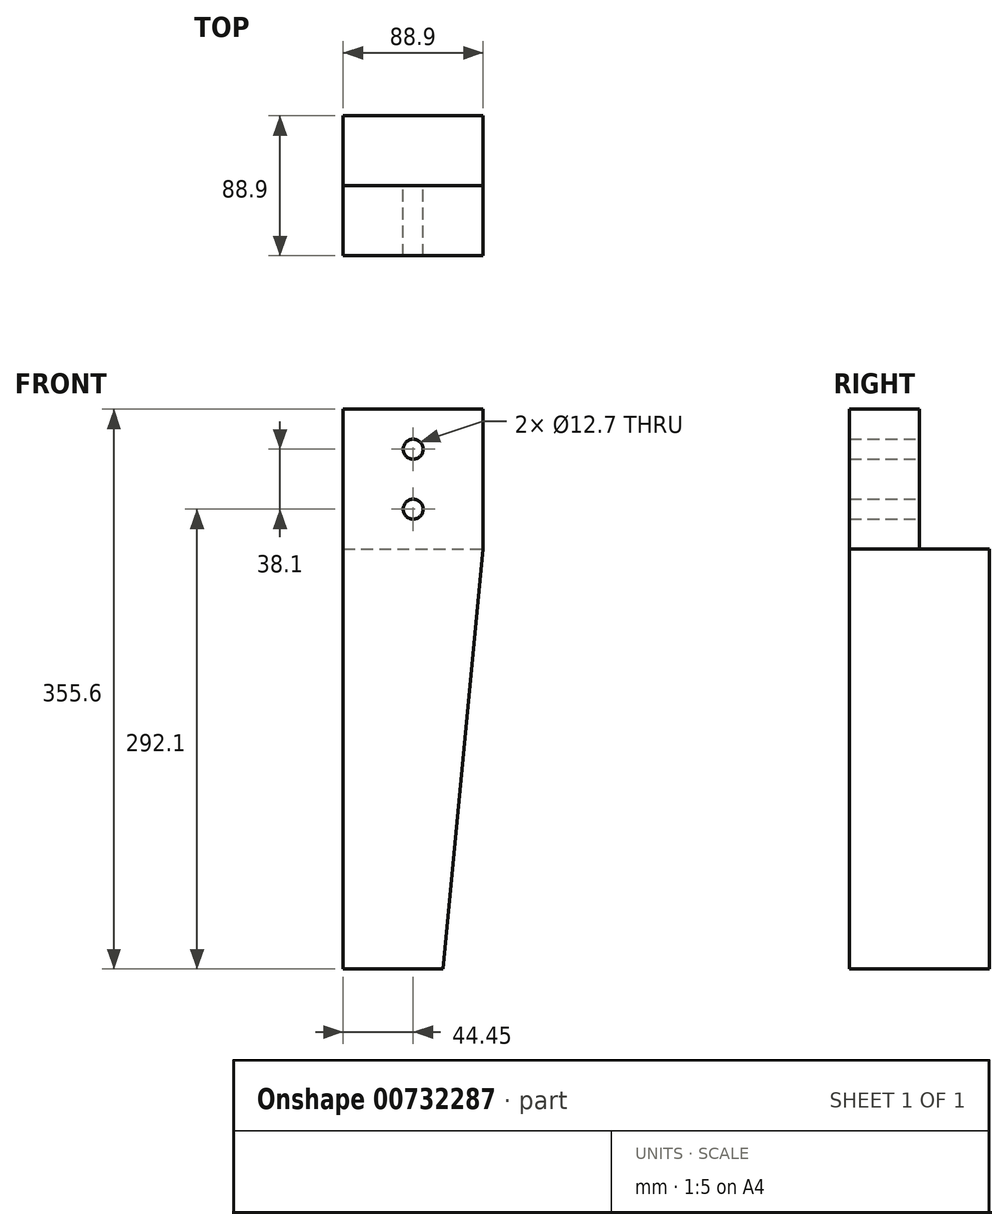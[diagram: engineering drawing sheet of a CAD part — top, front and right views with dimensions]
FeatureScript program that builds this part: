
annotation { "Feature Type Name" : "Feature", "Feature Type Description" : "" }
export const myFeature = defineFeature(function(context is Context, id is Id, definition is map)
    precondition{}
    {
        {
            var Q0;
            Q0=qCreatedBy(makeId("Front.planeOp"),FACE);
            var sketch = newSketch(context, id + "F0", { "sketchPlane" : qUnion([Q0])});
            skLineSegment(sketch, "E0.bottom", {"start": v(44.45, 177.8) * mm, "end": v(-44.45, 177.8) * mm});
            skLineSegment(sketch, "E0.top", {"start": v(44.45, -177.8) * mm, "end": v(-44.45, -177.8) * mm});
            skLineSegment(sketch, "E0.left", {"start": v(44.45, 177.8) * mm, "end": v(44.45, -177.8) * mm});
            skLineSegment(sketch, "E0.right", {"start": v(-44.45, 177.8) * mm, "end": v(-44.45, -177.8) * mm});
            skPoint(sketch, "E0.middle", {"position": v(0, 0) * mm});
            skLineSegment(sketch, "E1", {"start": v(-44.45, 88.9) * mm, "end": v(44.45, 88.9) * mm, "construction": true});
            skLineSegment(sketch, "E2", {"start": v(-19.05, 177.8) * mm, "end": v(-19.05, -177.8) * mm, "construction": true});
            skLineSegment(sketch, "E3", {"start": v(-44.45, 133.35) * mm, "end": v(44.45, 133.35) * mm, "construction": true});
            skLineSegment(sketch, "E4", {"start": v(-44.45, 152.4) * mm, "end": v(44.45, 152.4) * mm, "construction": true});
            skLineSegment(sketch, "E5", {"start": v(-44.45, 114.3) * mm, "end": v(44.45, 114.3) * mm, "construction": true});
            skLineSegment(sketch, "E6", {"start": v(0, 177.8) * mm, "end": v(0, 88.9) * mm, "construction": true});
            skCircle(sketch, "E7", {"center": v(0, 152.4) * mm, "radius": 6.35 * mm});
            skCircle(sketch, "E8", {"center": v(0, 114.3) * mm, "radius": 6.35 * mm});
            skLineSegment(sketch, "E9", {"start": v(19.05, 88.9) * mm, "end": v(19.05, -177.8) * mm, "construction": true});
            skLineSegment(sketch, "E10", {"start": v(44.45, 88.9) * mm, "end": v(19.05, -177.8) * mm});
            skSolve(sketch);
        }
        {
            var Q0;
            {var subQ1=sQuery(id+"F0.wireOp",EDGE,"E0.bottom");Q0=makeQuery(id+"F0.imprint","IMPRINT",FACE,{"disambiguationData":[TD([[makeQuery(id+"F0.imprint","IMPRINT",EDGE,{"derivedFrom":subQ1}),1.0]])]});}
            extrude(context, id + "F1", {"entities" : qUnion([Q0]), "depth" : 88.9 * mm, "offsetDistance" : 25.4 * mm});
        }
        {
            var Q0;
            Q0=makeQuery(id+"F1.opExtrude","SWEPT_FACE",FACE,{"disambiguationData":[OSD([sQuery(id+"F0.wireOp",EDGE,"E0.left")])]});
            var sketch = newSketch(context, id + "F2", { "sketchPlane" : qUnion([Q0])});
            skLineSegment(sketch, "E11", {"start": v(-44.45, 177.8) * mm, "end": v(-44.45, 88.9) * mm});
            skSolve(sketch);
        }
        {
            var Q0;
            {var subQ0=sQuery(id+"F2.wireOp",EDGE,"E11");Q0=makeQuery(id+"F2.imprint","IMPRINT",FACE,{"disambiguationData":[TD([[makeQuery(id+"F2.imprint","IMPRINT",EDGE,{"derivedFrom":subQ0}),1.0]])]});}
            extrude(context, id + "F3", {"entities" : qUnion([Q0]), "operationType" : NewBodyOperationType.REMOVE, "oppositeDirection" : true, "depth" : 101.6 * mm, "offsetDistance" : 25.4 * mm});
        }
    });
